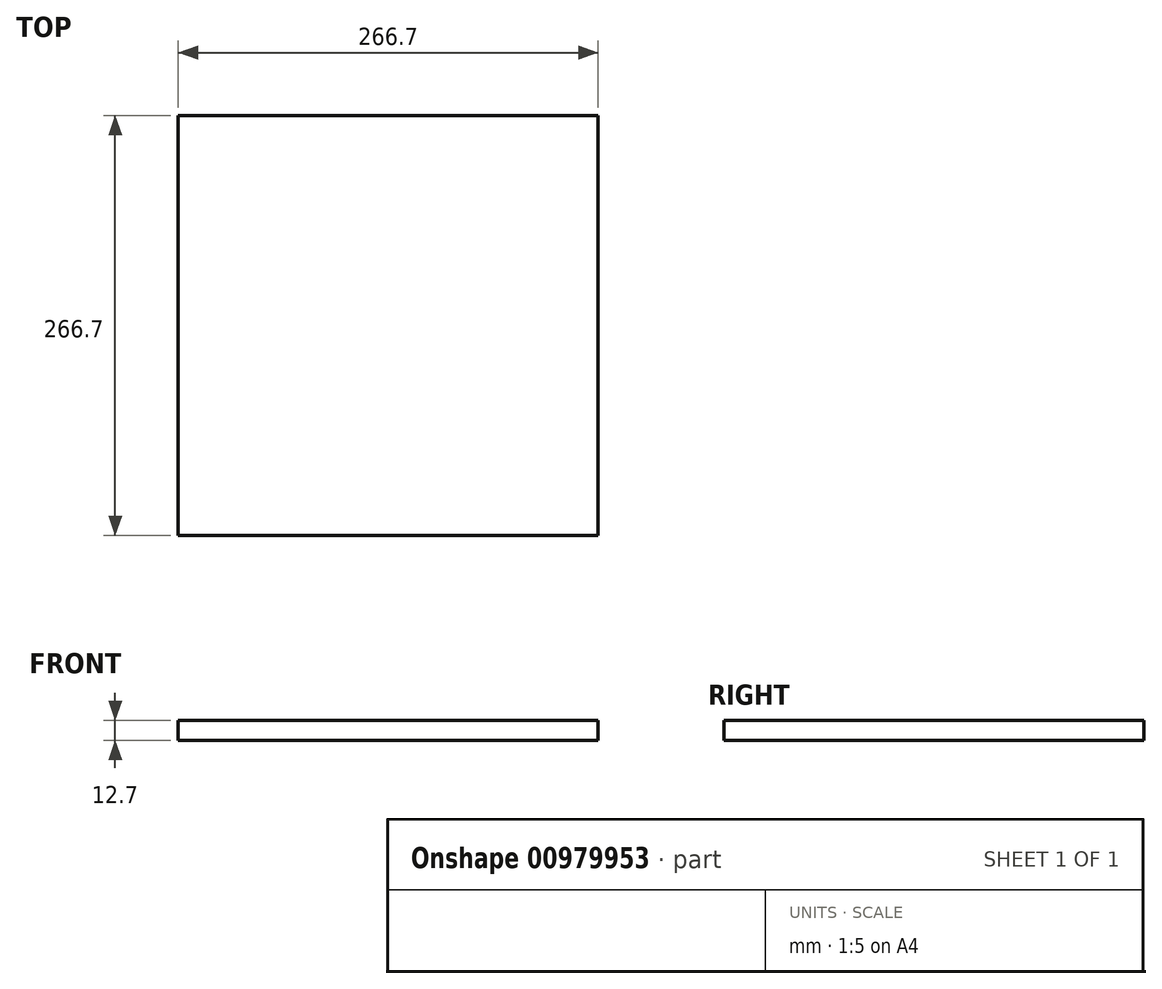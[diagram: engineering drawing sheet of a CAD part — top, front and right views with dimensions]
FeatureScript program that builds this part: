
annotation { "Feature Type Name" : "Feature", "Feature Type Description" : "" }
export const myFeature = defineFeature(function(context is Context, id is Id, definition is map)
    precondition{}
    {
        {
            var Q0;
            Q0=qCreatedBy(makeId("Top.planeOp"),FACE);
            var sketch = newSketch(context, id + "F0", { "sketchPlane" : qUnion([Q0])});
            skLineSegment(sketch, "E0.bottom", {"start": v(-133.35, 133.35) * mm, "end": v(133.35, 133.35) * mm});
            skLineSegment(sketch, "E0.top", {"start": v(-133.35, -133.35) * mm, "end": v(133.35, -133.35) * mm});
            skLineSegment(sketch, "E0.left", {"start": v(-133.35, 133.35) * mm, "end": v(-133.35, -133.35) * mm});
            skLineSegment(sketch, "E0.right", {"start": v(133.35, 133.35) * mm, "end": v(133.35, -133.35) * mm});
            skSolve(sketch);
        }
        {
            var Q0;
            Q0=qSketchRegion(id+"F0",true);
            extrude(context, id + "F1", {"entities" : qUnion([Q0]), "oppositeDirection" : true, "depth" : 12.7 * mm, "offsetDistance" : 25.4 * mm});
        }
    });
